# Revit family: Storage-Mounted-Teknion-BOSL_Wide_Overhead_Cabinet_Sliding_Doors-R2019
name_source: partatom
category: Casework
units: mm (PartAtom-declared; Revit-internal decimal feet)

## family parameters
Always vertical = Yes
Cut with Voids When Loaded = No
OmniClass Number = 23.40.70.14.64.21
OmniClass Title = Systems Furniture
Room Calculation Point = No
Shared = Yes
Work Plane-Based = No

## types (2) — shared parameters
Assembly Code = E2020200
Height = 14.567 "
Manufacturer = Teknion
Manufacturer Fax = 416.661.4586
Part Number = BOSL
Product Documentation Link = http://www.teknion.com
Product Line = Expansion Casegoods
Product Page URL = https://www.teknion.com
Series = Expansion Casegoods
Sustainability Data = http://www.teknion.com
URL = http://www.teknion.com
Unit Weight URL = http://www.teknion.com
Warranty = https://www.teknion.com

## per-type parameters (varying)
| type | Description | Model |
| Wall Mounted, 16"d x15"h | Overhead Cabinet - Solid Sliding Doors, Wall-Mounted Style, 16" Depth, 15" Height | BOSLW16__15 |
| Wall Panel Mounted, 16"d x15"h | Overhead Cabinet - Solid Sliding Doors, Wall Panel Mounted Style, 16" Depth, 15" Height | BOSLB16__15 |

## geometry (parser evidence)
native form markers: Blend x6, Sweep x2
no freeform markers — native parametric forms only
